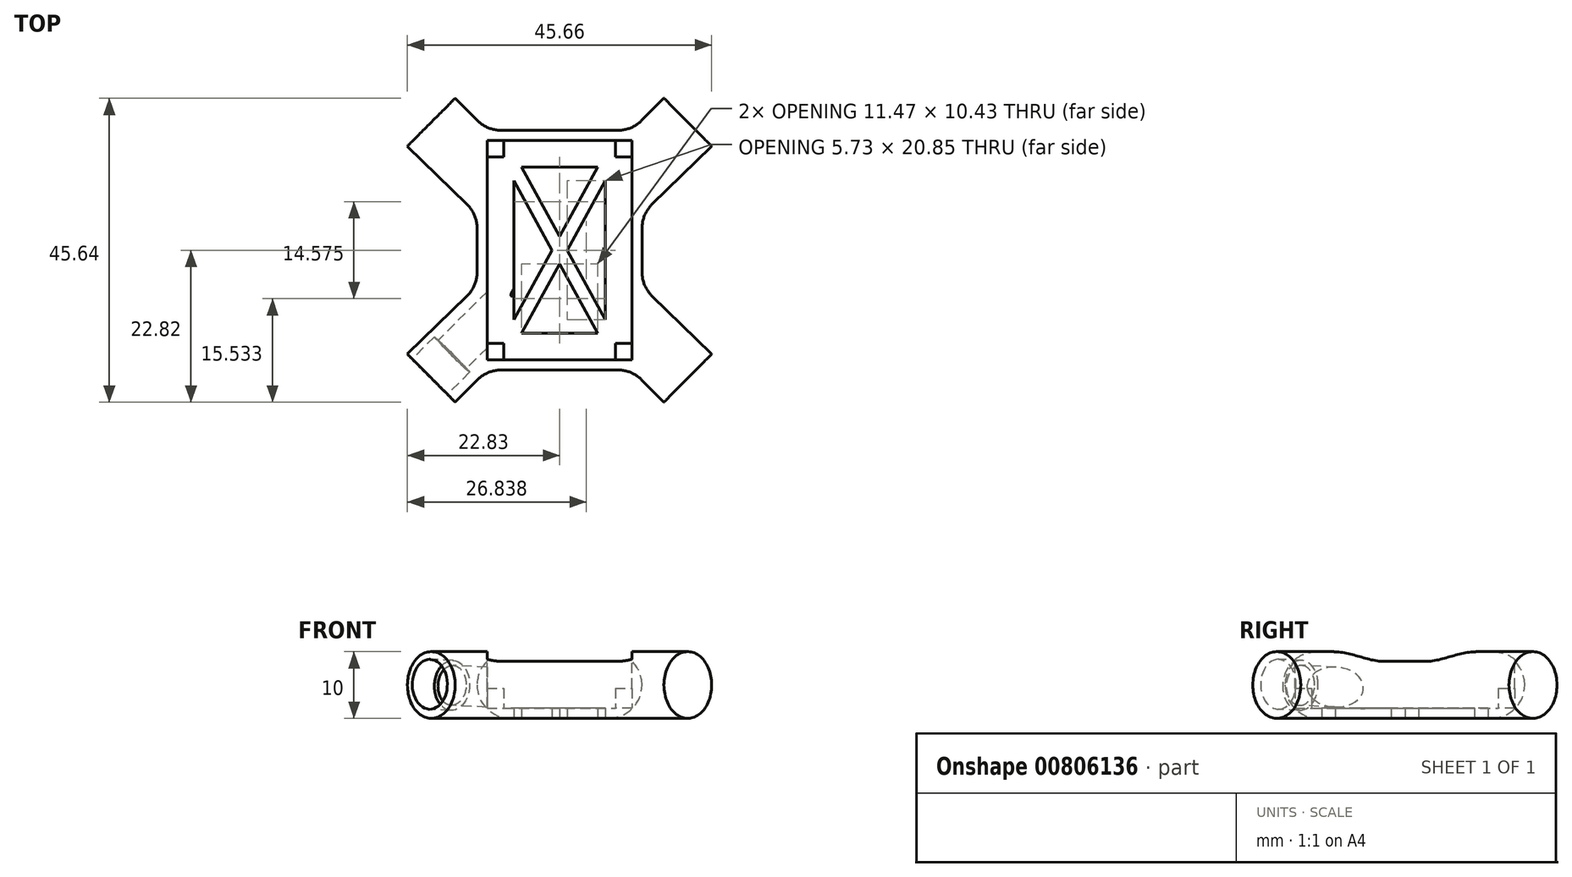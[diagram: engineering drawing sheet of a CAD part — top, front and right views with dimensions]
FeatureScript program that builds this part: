
annotation { "Feature Type Name" : "Feature", "Feature Type Description" : "" }
export const myFeature = defineFeature(function(context is Context, id is Id, definition is map)
    precondition{}
    {
        {
            var Q0;
            Q0=qCreatedBy(makeId("Top.planeOp"),FACE);
            var sketch = newSketch(context, id + "F0", { "sketchPlane" : qUnion([Q0])});
            skLineSegment(sketch, "E0.top", {"start": v(-10.88, -16.5) * mm, "end": v(0, -16.5) * mm});
            skLineSegment(sketch, "E1.bottom", {"start": v(-10.88, -16.5) * mm, "end": v(-9.38, -16.5) * mm});
            skLineSegment(sketch, "E1.left", {"start": v(-10.88, -16.5) * mm, "end": v(-10.88, -15) * mm});
            skLineSegment(sketch, "E2.3", {"start": v(-8.76, -18) * mm, "end": v(0, -18) * mm});
            skLineSegment(sketch, "E3", {"start": v(-22.83, -15.61) * mm, "end": v(-15.66, -22.82) * mm});
            skLineSegment(sketch, "E4.trimOffspring", {"start": v(-13.88, -6.87) * mm, "end": v(-22.83, -15.61) * mm});
            skLineSegment(sketch, "E5.trimOffspring", {"start": v(-12.3, -19.46) * mm, "end": v(-15.66, -22.82) * mm});
            skLineSegment(sketch, "E6.trimOffspring", {"start": v(-10.88, 0) * mm, "end": v(-10.88, -16.5) * mm});
            skLineSegment(sketch, "E7.trimOffspring", {"start": v(-12.38, 0) * mm, "end": v(-12.38, -3.3) * mm});
            skPoint(sketch, "E8.MirrorCS.end.orphan", {"position": v(0, -18) * mm});
            skCircle(sketch, "E9", {"center": v(0, 0) * mm, "radius": 50 * mm});
            skLineSegment(sketch, "E10", {"start": v(0, 50) * mm, "end": v(0, -50) * mm});
            skLineSegment(sketch, "E11", {"start": v(-50, 0) * mm, "end": v(50, 0) * mm});
            skLineSegment(sketch, "E12.MirrorCS", {"start": v(-10.88, 16.5) * mm, "end": v(-9.38, 16.5) * mm});
            skLineSegment(sketch, "E13.MirrorCS", {"start": v(-10.88, 16.5) * mm, "end": v(-10.88, 15) * mm});
            skLineSegment(sketch, "E14.MirrorCS", {"start": v(-10.88, 0) * mm, "end": v(-10.88, 16.5) * mm});
            skLineSegment(sketch, "E15.MirrorCS", {"start": v(-8.76, 18) * mm, "end": v(0, 18) * mm});
            skLineSegment(sketch, "E16.MirrorCS", {"start": v(-12.38, 0) * mm, "end": v(-12.38, 3.3) * mm});
            skLineSegment(sketch, "E17.MirrorCS", {"start": v(-22.83, 15.61) * mm, "end": v(-15.66, 22.82) * mm});
            skPoint(sketch, "E18.MirrorP", {"position": v(0, 18) * mm});
            skLineSegment(sketch, "E19.MirrorCS", {"start": v(-10.88, 16.5) * mm, "end": v(0, 16.5) * mm});
            skLineSegment(sketch, "E20.MirrorCS", {"start": v(-13.88, 6.87) * mm, "end": v(-22.83, 15.61) * mm});
            skLineSegment(sketch, "E21.MirrorCS", {"start": v(-12.3, 19.46) * mm, "end": v(-15.66, 22.82) * mm});
            skLineSegment(sketch, "E22.MirrorCS", {"start": v(10.88, -16.5) * mm, "end": v(9.38, -16.5) * mm});
            skLineSegment(sketch, "E23.MirrorCS", {"start": v(10.88, 16.5) * mm, "end": v(9.38, 16.5) * mm});
            skLineSegment(sketch, "E24.MirrorCS", {"start": v(10.88, 16.5) * mm, "end": v(10.88, 15) * mm});
            skLineSegment(sketch, "E25.MirrorCS", {"start": v(10.88, -16.5) * mm, "end": v(10.88, -15) * mm});
            skPoint(sketch, "E26.MirrorP", {"position": v(12.38, 0) * mm});
            skLineSegment(sketch, "E27.MirrorCS", {"start": v(8.76, -18) * mm, "end": v(0, -18) * mm});
            skLineSegment(sketch, "E28.MirrorCS", {"start": v(8.76, 18) * mm, "end": v(0, 18) * mm});
            skLineSegment(sketch, "E29.MirrorCS", {"start": v(12.38, 0) * mm, "end": v(12.38, 3.3) * mm});
            skLineSegment(sketch, "E30.MirrorCS", {"start": v(10.88, 0) * mm, "end": v(10.88, -16.5) * mm});
            skLineSegment(sketch, "E31.MirrorCS", {"start": v(22.83, -15.61) * mm, "end": v(15.66, -22.82) * mm});
            skLineSegment(sketch, "E32.MirrorCS", {"start": v(10.88, 16.5) * mm, "end": v(0, 16.5) * mm});
            skLineSegment(sketch, "E33.MirrorCS", {"start": v(12.3, 19.46) * mm, "end": v(15.66, 22.82) * mm});
            skLineSegment(sketch, "E34.MirrorCS", {"start": v(10.88, 0) * mm, "end": v(10.88, 16.5) * mm});
            skLineSegment(sketch, "E35.MirrorCS", {"start": v(13.88, 6.87) * mm, "end": v(22.83, 15.61) * mm});
            skLineSegment(sketch, "E36.MirrorCS", {"start": v(12.3, -19.46) * mm, "end": v(15.66, -22.82) * mm});
            skLineSegment(sketch, "E37.MirrorCS", {"start": v(13.88, -6.87) * mm, "end": v(22.83, -15.61) * mm});
            skLineSegment(sketch, "E38.MirrorCS", {"start": v(22.83, 15.61) * mm, "end": v(15.66, 22.82) * mm});
            skLineSegment(sketch, "E39.MirrorCS", {"start": v(10.88, -16.5) * mm, "end": v(0, -16.5) * mm});
            skLineSegment(sketch, "E40.MirrorCS", {"start": v(12.38, 0) * mm, "end": v(12.38, -3.3) * mm});
            skPoint(sketch, "E41.visualSharp", {"position": v(-10.83, -18) * mm});
            skArc(sketch, "E41.filletArc", {"start": v(-8.76, -18) * mm, "mid": v(-10.67, -18.38) * mm, "end": v(-12.3, -19.46) * mm});
            skPoint(sketch, "E42.visualSharp", {"position": v(-12.38, -5.4) * mm});
            skArc(sketch, "E42.filletArc", {"start": v(-13.88, -6.87) * mm, "mid": v(-12.77, -5.23) * mm, "end": v(-12.38, -3.3) * mm});
            skPoint(sketch, "E43.visualSharp", {"position": v(-12.38, 5.4) * mm});
            skArc(sketch, "E43.filletArc", {"start": v(-12.38, 3.3) * mm, "mid": v(-12.77, 5.23) * mm, "end": v(-13.88, 6.87) * mm});
            skPoint(sketch, "E44.visualSharp", {"position": v(12.38, -5.4) * mm});
            skArc(sketch, "E44.filletArc", {"start": v(12.38, -3.3) * mm, "mid": v(12.77, -5.23) * mm, "end": v(13.88, -6.87) * mm});
            skPoint(sketch, "E45.visualSharp", {"position": v(10.83, -18) * mm});
            skArc(sketch, "E45.filletArc", {"start": v(12.3, -19.46) * mm, "mid": v(10.67, -18.38) * mm, "end": v(8.76, -18) * mm});
            skPoint(sketch, "E46.visualSharp", {"position": v(12.38, 5.4) * mm});
            skArc(sketch, "E46.filletArc", {"start": v(13.88, 6.87) * mm, "mid": v(12.77, 5.23) * mm, "end": v(12.37, 3.3) * mm});
            skPoint(sketch, "E47.visualSharp", {"position": v(-10.83, 18) * mm});
            skArc(sketch, "E47.filletArc", {"start": v(-12.3, 19.46) * mm, "mid": v(-10.67, 18.38) * mm, "end": v(-8.76, 18) * mm});
            skPoint(sketch, "E48.visualSharp", {"position": v(10.83, 18) * mm});
            skArc(sketch, "E48.filletArc", {"start": v(8.76, 18) * mm, "mid": v(10.67, 18.38) * mm, "end": v(12.3, 19.46) * mm});
            skLineSegment(sketch, "E49.0", {"start": v(-6.87, 10.42) * mm, "end": v(-6.88, -10.42) * mm});
            skLineSegment(sketch, "E49.1", {"start": v(5.73, 12.5) * mm, "end": v(-5.73, 12.5) * mm});
            skLineSegment(sketch, "E49.2", {"start": v(6.88, -10.42) * mm, "end": v(6.87, 10.42) * mm});
            skLineSegment(sketch, "E49.3", {"start": v(-5.73, -12.5) * mm, "end": v(5.73, -12.5) * mm});
            skLineSegment(sketch, "E50.0", {"start": v(6.88, -10.42) * mm, "end": v(1.14, 0) * mm});
            skLineSegment(sketch, "E51.0", {"start": v(5.73, -12.5) * mm, "end": v(0, -2.08) * mm});
            skLineSegment(sketch, "E52.0", {"start": v(5.73, 12.5) * mm, "end": v(0, 2.08) * mm});
            skLineSegment(sketch, "E53.0", {"start": v(6.87, 10.42) * mm, "end": v(1.14, 0) * mm});
            skLineSegment(sketch, "E54.trimOffspring", {"start": v(0, -2.08) * mm, "end": v(-5.73, -12.5) * mm});
            skLineSegment(sketch, "E55.trimOffspring", {"start": v(0, 2.08) * mm, "end": v(-5.73, 12.5) * mm});
            skLineSegment(sketch, "E56.trimOffspring", {"start": v(-1.14, 0) * mm, "end": v(-6.88, -10.42) * mm});
            skLineSegment(sketch, "E57.trimOffspring", {"start": v(-1.14, 0) * mm, "end": v(-6.87, 10.42) * mm});
            skSolve(sketch);
        }
        {
            var Q0;
            Q0=makeQuery(id+"F0.imprint","IMPRINT",FACE,{"disambiguationData":[TD([[makeQuery(id+"F0.imprint","IMPRINT",EDGE,{"derivedFrom":sQuery(id+"F0.wireOp",EDGE,"E23.MirrorCS")}),-1.0]])]});
            var Q1;
            Q1=makeQuery(id+"F0.imprint","IMPRINT",FACE,{"disambiguationData":[TD([[makeQuery(id+"F0.imprint","IMPRINT",EDGE,{"derivedFrom":sQuery(id+"F0.wireOp",EDGE,"E12.MirrorCS")}),1.0]])]});
            var Q2;
            {var subQ7=sQuery(id+"F0.wireOp",EDGE,"E1.left");Q2=makeQuery(id+"F0.imprint","IMPRINT",FACE,{"disambiguationData":[TD([[makeQuery(id+"F0.imprint","IMPRINT",EDGE,{"derivedFrom":subQ7}),1.0]])]});}
            var Q3;
            Q3=makeQuery(id+"F0.imprint","IMPRINT",FACE,{"disambiguationData":[TD([[makeQuery(id+"F0.imprint","IMPRINT",EDGE,{"derivedFrom":sQuery(id+"F0.wireOp",EDGE,"E22.MirrorCS")}),1.0]])]});
            var Q4;
            Q4=makeQuery(id+"F0.imprint","IMPRINT",FACE,{"disambiguationData":[TD([[makeQuery(id+"F0.imprint","IMPRINT",EDGE,{"derivedFrom":sQuery(id+"F0.wireOp",EDGE,"E12.MirrorCS")}),-1.0]])]});
            var Q5;
            Q5=makeQuery(id+"F0.imprint","IMPRINT",FACE,{"disambiguationData":[TD([[makeQuery(id+"F0.imprint","IMPRINT",EDGE,{"derivedFrom":sQuery(id+"F0.wireOp",EDGE,"E23.MirrorCS")}),1.0]])]});
            var Q6;
            Q6=makeQuery(id+"F0.imprint","IMPRINT",FACE,{"disambiguationData":[TD([[makeQuery(id+"F0.imprint","IMPRINT",EDGE,{"derivedFrom":sQuery(id+"F0.wireOp",EDGE,"E22.MirrorCS")}),-1.0]])]});
            var Q7;
            {var subQ6=sQuery(id+"F0.wireOp",EDGE,"E1.left");Q7=makeQuery(id+"F0.imprint","IMPRINT",FACE,{"disambiguationData":[TD([[makeQuery(id+"F0.imprint","IMPRINT",EDGE,{"derivedFrom":subQ6}),-1.0]])]});}
            extrude(context, id + "F1", {"entities" : qUnion([Q0, Q1, Q2, Q3, Q4, Q5, Q6, Q7]), "depth" : 10 * mm, "offsetDistance" : 25 * mm});
        }
        {
            var Q0;
            Q0=makeQuery(id+"F0.imprint","IMPRINT",FACE,{"disambiguationData":[TD([[makeQuery(id+"F0.imprint","IMPRINT",EDGE,{"derivedFrom":sQuery(id+"F0.wireOp",EDGE,"E12.MirrorCS")}),-1.0]])]});
            var Q1;
            Q1=makeQuery(id+"F0.imprint","IMPRINT",FACE,{"disambiguationData":[TD([[makeQuery(id+"F0.imprint","IMPRINT",EDGE,{"derivedFrom":sQuery(id+"F0.wireOp",EDGE,"E23.MirrorCS")}),1.0]])]});
            var Q2;
            Q2=makeQuery(id+"F0.imprint","IMPRINT",FACE,{"disambiguationData":[TD([[makeQuery(id+"F0.imprint","IMPRINT",EDGE,{"derivedFrom":sQuery(id+"F0.wireOp",EDGE,"E1.top")}),-1.0]])]});
            var Q3;
            Q3=makeQuery(id+"F0.imprint","IMPRINT",FACE,{"disambiguationData":[TD([[makeQuery(id+"F0.imprint","IMPRINT",EDGE,{"derivedFrom":sQuery(id+"F0.wireOp",EDGE,"E22.MirrorCS")}),-1.0]])]});
            var Q4;
            {var subQ1=sQuery(id+"F0.wireOp",EDGE,"E1.left");Q4=makeQuery(id+"F0.imprint","IMPRINT",FACE,{"disambiguationData":[TD([[makeQuery(id+"F0.imprint","IMPRINT",EDGE,{"derivedFrom":subQ1}),-1.0]])]});}
            extrude(context, id + "F2", {"entities" : qUnion([Q0, Q1, Q2, Q3, Q4]), "operationType" : NewBodyOperationType.ADD, "depth" : 1 * mm, "offsetDistance" : 25 * mm});
        }
        {
            var Q0;
            Q0=makeQuery(id+"F1.opExtrude","SWEPT_FACE",FACE,{"disambiguationData":[OSD([sQuery(id+"F0.wireOp",EDGE,"E3")])]});
            var sketch = newSketch(context, id + "F3", { "sketchPlane" : qUnion([Q0])});
            skCircle(sketch, "E58", {"center": v(0.03, 5) * mm, "radius": 3.75 * mm});
            skCircle(sketch, "E59.0", {"center": v(0.03, 5) * mm, "radius": 2.75 * mm});
            skLineSegment(sketch, "E60", {"start": v(3.78, 5) * mm, "end": v(-6.37, 5) * mm, "construction": true});
            skSolve(sketch);
        }
        {
            var Q0;
            Q0=makeQuery(id+"F3.imprint","IMPRINT",FACE,{"disambiguationData":[TD([[makeQuery(id+"F3.imprint","IMPRINT",EDGE,{"derivedFrom":sQuery(id+"F3.wireOp",EDGE,"E58")}),-1.0]])]});
            var Q1;
            Q1=sQuery(id+"F3.wireOp",EDGE,"E60");
            cPlane(context, id + "F4", {"entities" : qUnion([Q0, Q1]), "cplaneType" : CPlaneType.LINE_ANGLE, "offset" : 25 * mm, "angle" : 2 * degree, "width" : 150 * mm, "height" : 150 * mm});
        }
        {
            var Q0;
            Q0=qCreatedBy(id+"F4.planeOp",FACE);
            var sketch = newSketch(context, id + "F5", { "sketchPlane" : qUnion([Q0])});
            skCircle(sketch, "E61", {"center": v(0.11, 4.16) * mm, "radius": 3.75 * mm});
            skCircle(sketch, "E62.0", {"center": v(0.11, 4.16) * mm, "radius": 3 * mm});
            skSolve(sketch);
        }
        {
            var Q0;
            Q0=makeQuery(id+"F5.imprint","IMPRINT",FACE,{"disambiguationData":[TD([[makeQuery(id+"F5.imprint","IMPRINT",EDGE,{"derivedFrom":sQuery(id+"F5.wireOp",EDGE,"E62.0")}),1.0]])]});
            extrude(context, id + "F6", {"entities" : qUnion([Q0]), "operationType" : NewBodyOperationType.REMOVE, "depth" : 21.17 * mm, "offsetDistance" : 25 * mm, "hasSecondDirection" : true, "secondDirectionOppositeDirection" : true, "secondDirectionDepth" : 25 * mm});
        }
        {
            var Q0;
            Q0=makeQuery(id+"F5.imprint","IMPRINT",FACE,{"disambiguationData":[TD([[makeQuery(id+"F5.imprint","IMPRINT",EDGE,{"derivedFrom":sQuery(id+"F5.wireOp",EDGE,"E61")}),1.0]])]});
            extrude(context, id + "F7", {"entities" : qUnion([Q0]), "operationType" : NewBodyOperationType.REMOVE, "depth" : 4.7 * mm, "offsetDistance" : 25 * mm, "hasSecondDirection" : true, "secondDirectionOppositeDirection" : true, "secondDirectionDepth" : 25 * mm});
        }
        {
            var Q0;
            Q0=makeQuery(id+"F1.opExtrude","CAP_EDGE",EDGE,{"disambiguationData":[OSD([sQuery(id+"F0.wireOp",EDGE,"E5.trimOffspring")])],"isStart":false});
            var Q1;
            Q1=makeQuery(id+"F1.opExtrude","CAP_EDGE",EDGE,{"disambiguationData":[OSD([sQuery(id+"F0.wireOp",EDGE,"E41.filletArc")])],"isStart":false});
            var Q2;
            Q2=makeQuery(id+"F1.opExtrude","CAP_EDGE",EDGE,{"disambiguationData":[OSD([sQuery(id+"F0.wireOp",EDGE,"E2.3"),sQuery(id+"F0.wireOp",EDGE,"E27.MirrorCS")])],"isStart":false});
            var Q3;
            Q3=makeQuery(id+"F1.opExtrude","CAP_EDGE",EDGE,{"disambiguationData":[OSD([sQuery(id+"F0.wireOp",EDGE,"E45.filletArc")])],"isStart":false});
            var Q4;
            Q4=makeQuery(id+"F1.opExtrude","CAP_EDGE",EDGE,{"disambiguationData":[OSD([sQuery(id+"F0.wireOp",EDGE,"E36.MirrorCS")])],"isStart":false});
            var Q5;
            Q5=makeQuery(id+"F1.opExtrude","CAP_EDGE",EDGE,{"disambiguationData":[OSD([sQuery(id+"F0.wireOp",EDGE,"E37.MirrorCS")])],"isStart":false});
            var Q6;
            Q6=makeQuery(id+"F1.opExtrude","CAP_EDGE",EDGE,{"disambiguationData":[OSD([sQuery(id+"F0.wireOp",EDGE,"E44.filletArc")])],"isStart":false});
            var Q7;
            Q7=makeQuery(id+"F1.opExtrude","CAP_EDGE",EDGE,{"disambiguationData":[OSD([sQuery(id+"F0.wireOp",EDGE,"E29.MirrorCS"),sQuery(id+"F0.wireOp",EDGE,"E40.MirrorCS")])],"isStart":false});
            var Q8;
            Q8=makeQuery(id+"F1.opExtrude","CAP_EDGE",EDGE,{"disambiguationData":[OSD([sQuery(id+"F0.wireOp",EDGE,"E46.filletArc")])],"isStart":false});
            var Q9;
            Q9=makeQuery(id+"F1.opExtrude","CAP_EDGE",EDGE,{"disambiguationData":[OSD([sQuery(id+"F0.wireOp",EDGE,"E35.MirrorCS")])],"isStart":false});
            var Q10;
            Q10=makeQuery(id+"F1.opExtrude","CAP_EDGE",EDGE,{"disambiguationData":[OSD([sQuery(id+"F0.wireOp",EDGE,"E4.trimOffspring")])],"isStart":false});
            var Q11;
            Q11=makeQuery(id+"F1.opExtrude","CAP_EDGE",EDGE,{"disambiguationData":[OSD([sQuery(id+"F0.wireOp",EDGE,"E42.filletArc")])],"isStart":false});
            var Q12;
            Q12=makeQuery(id+"F1.opExtrude","CAP_EDGE",EDGE,{"disambiguationData":[OSD([sQuery(id+"F0.wireOp",EDGE,"E7.trimOffspring"),sQuery(id+"F0.wireOp",EDGE,"E16.MirrorCS")])],"isStart":false});
            var Q13;
            Q13=makeQuery(id+"F1.opExtrude","CAP_EDGE",EDGE,{"disambiguationData":[OSD([sQuery(id+"F0.wireOp",EDGE,"E43.filletArc")])],"isStart":false});
            var Q14;
            Q14=makeQuery(id+"F1.opExtrude","CAP_EDGE",EDGE,{"disambiguationData":[OSD([sQuery(id+"F0.wireOp",EDGE,"E20.MirrorCS")])],"isStart":false});
            var Q15;
            Q15=makeQuery(id+"F1.opExtrude","CAP_EDGE",EDGE,{"disambiguationData":[OSD([sQuery(id+"F0.wireOp",EDGE,"E21.MirrorCS")])],"isStart":false});
            var Q16;
            Q16=makeQuery(id+"F1.opExtrude","CAP_EDGE",EDGE,{"disambiguationData":[OSD([sQuery(id+"F0.wireOp",EDGE,"E47.filletArc")])],"isStart":false});
            var Q17;
            Q17=makeQuery(id+"F1.opExtrude","CAP_EDGE",EDGE,{"disambiguationData":[OSD([sQuery(id+"F0.wireOp",EDGE,"E15.MirrorCS"),sQuery(id+"F0.wireOp",EDGE,"E28.MirrorCS")])],"isStart":false});
            var Q18;
            Q18=makeQuery(id+"F1.opExtrude","CAP_EDGE",EDGE,{"disambiguationData":[OSD([sQuery(id+"F0.wireOp",EDGE,"E48.filletArc")])],"isStart":false});
            var Q19;
            Q19=makeQuery(id+"F1.opExtrude","CAP_EDGE",EDGE,{"disambiguationData":[OSD([sQuery(id+"F0.wireOp",EDGE,"E33.MirrorCS")])],"isStart":false});
            fillet(context, id + "F8", {"entities" : qUnion([Q0, Q1, Q2, Q3, Q4, Q5, Q6, Q7, Q8, Q9, Q10, Q11, Q12, Q13, Q14, Q15, Q16, Q17, Q18, Q19]), "tangentPropagation" : true, "radius" : 5 * mm, "defaultsChanged" : false, "vertexSettings" : [], "allowEdgeOverflow" : false});
        }
        {
            var Q0;
            Q0=makeQuery(id+"F1.opExtrude","CAP_EDGE",EDGE,{"disambiguationData":[OSD([sQuery(id+"F0.wireOp",EDGE,"E37.MirrorCS")])],"isStart":true});
            var Q1;
            Q1=makeQuery(id+"F1.opExtrude","CAP_EDGE",EDGE,{"disambiguationData":[OSD([sQuery(id+"F0.wireOp",EDGE,"E2.3"),sQuery(id+"F0.wireOp",EDGE,"E27.MirrorCS")])],"isStart":true});
            var Q2;
            Q2=makeQuery(id+"F1.opExtrude","CAP_EDGE",EDGE,{"disambiguationData":[OSD([sQuery(id+"F0.wireOp",EDGE,"E4.trimOffspring")])],"isStart":true});
            var Q3;
            Q3=makeQuery(id+"F1.opExtrude","CAP_EDGE",EDGE,{"disambiguationData":[OSD([sQuery(id+"F0.wireOp",EDGE,"E15.MirrorCS"),sQuery(id+"F0.wireOp",EDGE,"E28.MirrorCS")])],"isStart":true});
            fillet(context, id + "F9", {"entities" : qUnion([Q0, Q1, Q2, Q3]), "tangentPropagation" : true, "radius" : 5 * mm, "defaultsChanged" : true, "vertexSettings" : [], "allowEdgeOverflow" : false});
        }
        {
            var Q0;
            Q0=makeQuery(id+"F1.opExtrude","CAP_FACE",FACE,{"disambiguationData":[OSD([sQuery(id+"F0.wireOp",EDGE,"E2.3"),sQuery(id+"F0.wireOp",EDGE,"E3"),sQuery(id+"F0.wireOp",EDGE,"E4.trimOffspring"),sQuery(id+"F0.wireOp",EDGE,"E5.trimOffspring"),sQuery(id+"F0.wireOp",EDGE,"E7.trimOffspring"),sQuery(id+"F0.wireOp",EDGE,"E15.MirrorCS"),sQuery(id+"F0.wireOp",EDGE,"E16.MirrorCS"),sQuery(id+"F0.wireOp",EDGE,"E17.MirrorCS"),sQuery(id+"F0.wireOp",EDGE,"E20.MirrorCS"),sQuery(id+"F0.wireOp",EDGE,"E21.MirrorCS"),sQuery(id+"F0.wireOp",EDGE,"E27.MirrorCS"),sQuery(id+"F0.wireOp",EDGE,"E28.MirrorCS"),sQuery(id+"F0.wireOp",EDGE,"E29.MirrorCS"),sQuery(id+"F0.wireOp",EDGE,"E31.MirrorCS"),sQuery(id+"F0.wireOp",EDGE,"E33.MirrorCS"),sQuery(id+"F0.wireOp",EDGE,"E35.MirrorCS"),sQuery(id+"F0.wireOp",EDGE,"E36.MirrorCS"),sQuery(id+"F0.wireOp",EDGE,"E37.MirrorCS"),sQuery(id+"F0.wireOp",EDGE,"E38.MirrorCS"),sQuery(id+"F0.wireOp",EDGE,"E40.MirrorCS"),sQuery(id+"F0.wireOp",EDGE,"E41.filletArc"),sQuery(id+"F0.wireOp",EDGE,"E42.filletArc"),sQuery(id+"F0.wireOp",EDGE,"E43.filletArc"),sQuery(id+"F0.wireOp",EDGE,"E44.filletArc"),sQuery(id+"F0.wireOp",EDGE,"E45.filletArc"),sQuery(id+"F0.wireOp",EDGE,"E46.filletArc"),sQuery(id+"F0.wireOp",EDGE,"E47.filletArc"),sQuery(id+"F0.wireOp",EDGE,"E48.filletArc"),sQuery(id+"F0.wireOp",EDGE,"E49.0"),sQuery(id+"F0.wireOp",EDGE,"E49.1"),sQuery(id+"F0.wireOp",EDGE,"E49.2"),sQuery(id+"F0.wireOp",EDGE,"E49.3"),sQuery(id+"F0.wireOp",EDGE,"E50.0"),sQuery(id+"F0.wireOp",EDGE,"E51.0"),sQuery(id+"F0.wireOp",EDGE,"E52.0"),sQuery(id+"F0.wireOp",EDGE,"E53.0"),sQuery(id+"F0.wireOp",EDGE,"E54.trimOffspring"),sQuery(id+"F0.wireOp",EDGE,"E55.trimOffspring"),sQuery(id+"F0.wireOp",EDGE,"E56.trimOffspring"),sQuery(id+"F0.wireOp",EDGE,"E57.trimOffspring")])],"isStart":false});
            var sketch = newSketch(context, id + "F10", { "sketchPlane" : qUnion([Q0])});
            skLineSegment(sketch, "E63.0", {"start": v(10.88, 16.5) * mm, "end": v(0, 16.5) * mm});
            skLineSegment(sketch, "E63.1", {"start": v(-10.88, 16.5) * mm, "end": v(0, 16.5) * mm});
            skLineSegment(sketch, "E63.2", {"start": v(-10.88, 0) * mm, "end": v(-10.88, 16.5) * mm});
            skLineSegment(sketch, "E63.3", {"start": v(-10.88, 0) * mm, "end": v(-10.88, -16.5) * mm});
            skLineSegment(sketch, "E63.4", {"start": v(-10.88, -16.5) * mm, "end": v(0, -16.5) * mm});
            skLineSegment(sketch, "E63.5", {"start": v(10.88, -16.5) * mm, "end": v(0, -16.5) * mm});
            skLineSegment(sketch, "E63.6", {"start": v(10.88, 0) * mm, "end": v(10.88, -16.5) * mm});
            skLineSegment(sketch, "E63.7", {"start": v(10.88, 0) * mm, "end": v(10.88, 16.5) * mm});
            skSolve(sketch);
        }
        {
            var Q0;
            Q0 = qSketchRegion(id + "F10", true);
            extrude(context, id + "F11", {"entities" : qUnion([Q0]), "operationType" : NewBodyOperationType.REMOVE, "oppositeDirection" : true, "depth" : 8.5 * mm, "offsetDistance" : 25 * mm});
        }
        {
            var Q0;
            Q0=makeQuery(id+"F11.boolean.opBoolean","COPY",FACE,{"derivedFrom":makeQuery(id+"F11.opExtrude","CAP_FACE",FACE,{"disambiguationData":[OSD([sQuery(id+"F10.wireOp",EDGE,"E63.0"),sQuery(id+"F10.wireOp",EDGE,"E63.1"),sQuery(id+"F10.wireOp",EDGE,"E63.2"),sQuery(id+"F10.wireOp",EDGE,"E63.3"),sQuery(id+"F10.wireOp",EDGE,"E63.4"),sQuery(id+"F10.wireOp",EDGE,"E63.5"),sQuery(id+"F10.wireOp",EDGE,"E63.6"),sQuery(id+"F10.wireOp",EDGE,"E63.7")])],"isStart":false})});
            var sketch = newSketch(context, id + "F12", { "sketchPlane" : qUnion([Q0])});
            skLineSegment(sketch, "E64.bottom", {"start": v(-10.88, 16.5) * mm, "end": v(-8.38, 16.5) * mm});
            skLineSegment(sketch, "E64.top", {"start": v(-10.88, 14) * mm, "end": v(-8.38, 14) * mm});
            skLineSegment(sketch, "E64.left", {"start": v(-10.88, 16.5) * mm, "end": v(-10.88, 14) * mm});
            skLineSegment(sketch, "E64.right", {"start": v(-8.38, 16.5) * mm, "end": v(-8.38, 14) * mm});
            skLineSegment(sketch, "E65.MirrorCS", {"start": v(-8.38, -16.5) * mm, "end": v(-8.38, -14) * mm});
            skLineSegment(sketch, "E66.MirrorCS", {"start": v(-10.88, -14) * mm, "end": v(-8.38, -14) * mm});
            skLineSegment(sketch, "E67.MirrorCS", {"start": v(8.38, 16.5) * mm, "end": v(8.38, 14) * mm});
            skLineSegment(sketch, "E68.MirrorCS", {"start": v(10.88, 14) * mm, "end": v(8.38, 14) * mm});
            skLineSegment(sketch, "E69.MirrorCS", {"start": v(10.88, -14) * mm, "end": v(8.38, -14) * mm});
            skLineSegment(sketch, "E70.MirrorCS", {"start": v(8.38, -16.5) * mm, "end": v(8.38, -14) * mm});
            skSolve(sketch);
        }
        {
            var Q0;
            {var subQ0=sQuery(id+"F12.wireOp",EDGE,"E67.MirrorCS");Q0=makeQuery(id+"F12.imprint","IMPRINT",FACE,{"disambiguationData":[TD([[makeQuery(id+"F12.imprint","IMPRINT",EDGE,{"derivedFrom":subQ0}),1.0]])]});}
            var Q1;
            {var subQ0=sQuery(id+"F12.wireOp",EDGE,"E69.MirrorCS");Q1=makeQuery(id+"F12.imprint","IMPRINT",FACE,{"disambiguationData":[TD([[makeQuery(id+"F12.imprint","IMPRINT",EDGE,{"derivedFrom":subQ0}),1.0]])]});}
            var Q2;
            {var subQ0=sQuery(id+"F12.wireOp",EDGE,"E65.MirrorCS");Q2=makeQuery(id+"F12.imprint","IMPRINT",FACE,{"disambiguationData":[TD([[makeQuery(id+"F12.imprint","IMPRINT",EDGE,{"derivedFrom":subQ0}),1.0]])]});}
            var Q3;
            Q3=makeQuery(id+"F12.imprint","IMPRINT",FACE,{"disambiguationData":[TD([[makeQuery(id+"F12.imprint","IMPRINT",EDGE,{"derivedFrom":sQuery(id+"F12.wireOp",EDGE,"E64.bottom")}),1.0]])]});
            extrude(context, id + "F13", {"entities" : qUnion([Q0, Q1, Q2, Q3]), "operationType" : NewBodyOperationType.ADD, "depth" : 3 * mm, "offsetDistance" : 25 * mm});
        }
    });
